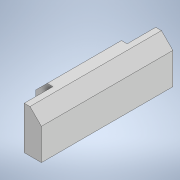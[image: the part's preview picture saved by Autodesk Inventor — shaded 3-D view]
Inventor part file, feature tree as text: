
AUTODESK INVENTOR PART (.ipt)
format: ipt  version: 2021 (Build 250183000, 183)  size: 126,464 bytes
history: native  units: in
note: dims shown in document units (in); Inventor stores cm internally (conversion verified against a paired STEP export)
features: extrude x3, sketch x3
ambient origin geometry x8: Origin, YZ Plane, XZ Plane, XY Plane, X Axis, Y Axis, Z Axis, Center Point
bodies: Solid1 (feature_tree)
feature tree (6):
  extrude  "Extrusion1"  Depth=0.2362in
  extrude  "Extrusion2"  Depth=0.5906in
  extrude  "Extrusion3"  Depth=0.1181in
  sketch  "Sketch1"  dims[d0=0.2362in d1=0.4331in]
  sketch  "Sketch2"  dims[d2=0.5906in d3=0.0787in]
  sketch  "Sketch3"  dims[d4=0.3937in d5=0.0in d6=0.1181in d7=1.0236in d8=0.0in d9=0.3937in d10=0.0in]
